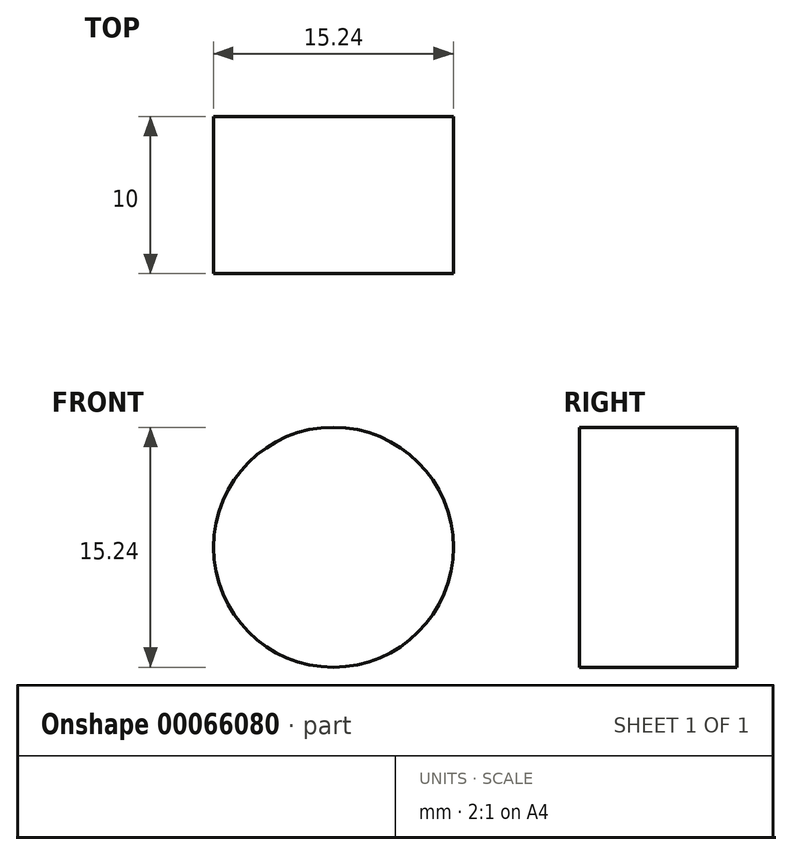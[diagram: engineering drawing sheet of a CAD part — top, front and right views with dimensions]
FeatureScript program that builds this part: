
annotation { "Feature Type Name" : "Feature", "Feature Type Description" : "" }
export const myFeature = defineFeature(function(context is Context, id is Id, definition is map)
    precondition{}
    {
        {
            var Q0;
            Q0=qCreatedBy(makeId("Front.planeOp"),FACE);
            var sketch = newSketch(context, id + "F0", { "sketchPlane" : qUnion([Q0])});
            skPoint(sketch, "E0.rect.middle", {"position": v(-1.07, 28.52) * mm});
            skCircle(sketch, "E1", {"center": v(0, 0) * mm, "radius": 7.62 * mm});
            skSolve(sketch);
        }
        {
            var Q0;
            Q0 = qSketchRegion(id + "F0", true);
            extrude(context, id + "F1", {"entities" : qUnion([Q0]), "depth" : 10 * mm});
        }
    });
